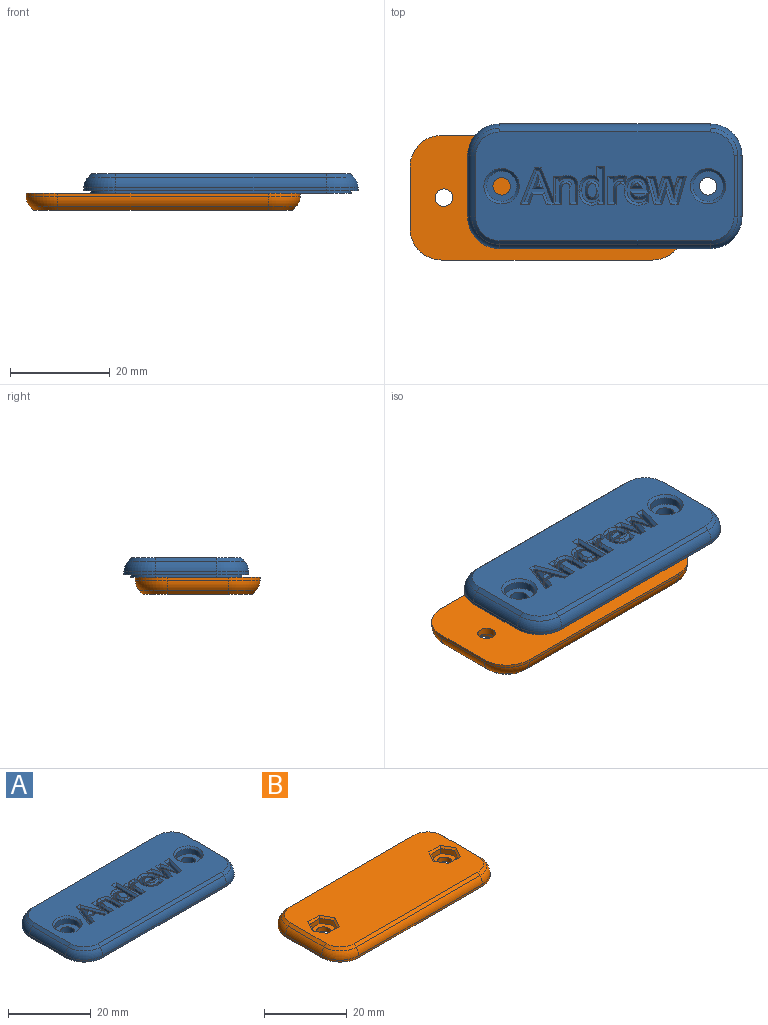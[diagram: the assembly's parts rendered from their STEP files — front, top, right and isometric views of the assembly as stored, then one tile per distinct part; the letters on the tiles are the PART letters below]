
ASSEMBLY  parts=2 mates=1
PART A: 259 faces, bbox 56.4x26.4x4.5 mm
  f0: plane 6.36x5.62mm, normal (0,0,1), area 10.3mm2, adj f87,f88,f89,f90,f91,f92,f93,f99
  f1: plane 4.93x4.02mm, normal (0,0,1), area 9mm2, adj f62,f63,f64,f65,f66,f67,f68,f69
  f2: plane 6.83x4.18mm, normal (0,0,1), area 11mm2, adj f26,f27,f28,f29,f30,f31,f32,f33
  f3: plane 12.3x0.56mm, normal (-1,0,0), area 6.9mm2, adj f4,f100,f102,f114
  f4: cylinder r=6.35mm len=6.35mm, axis (0,0,-1), area 5.6mm2, adj f3,f5,f102,f112
  f5: plane 42.3x0.56mm, normal (0,-1,0), area 23.6mm2, adj f4,f6,f102,f111
  f6: cylinder r=6.35mm len=6.35mm, axis (0,0,-1), area 5.6mm2, adj f5,f7,f102,f113
  f7: plane 12.3x0.56mm, normal (1,0,0), area 6.9mm2, adj f6,f8,f102,f115
  f8: cylinder r=6.35mm len=6.35mm, axis (0,0,-1), area 5.6mm2, adj f7,f9,f102,f117
  f9: plane 42.3x0.56mm, normal (0,1,0), area 23.6mm2, adj f8,f100,f102,f118
  f10: plane 2.9x0.72mm, normal (0,1,0), area 2.1mm2, adj f11,f94,f136,f207
  f11: plane 3.07x2.9mm, normal (1,0,0), area 8.9mm2, adj f10,f12,f136,f211
  f12: extruded ~2.9x0.87mm, area 2.7mm2, adj f11,f13,f136,f215
  f13: extruded ~2.9x0.83mm, area 2.6mm2, adj f12,f14,f136,f219
  f14: extruded ~2.9x1.09mm, area 3.5mm2, adj f13,f15,f136,f223
  f15: extruded ~2.9x1.33mm, area 4.1mm2, adj f14,f16,f136,f226
  f16: plane 2.9x2.49mm, normal (-1,0,0), area 7.2mm2, adj f15,f17,f136,f228
  f17: plane 2.9x0.72mm, normal (0,1,0), area 2.1mm2, adj f16,f18,f136,f227
  f18: plane 4.75x2.9mm, normal (1,0,0), area 13.8mm2, adj f17,f19,f136,f225
  f19: plane 2.9x0.59mm, normal (0,-1,0), area 1.7mm2, adj f18,f20,f136,f222
  f20: plane 2.9x0.65mm, normal (-0.98,-0.18,0), area 1.9mm2, adj f19,f21,f136,f218
  f21: plane 2.92x0.04mm, normal (0,-1,0), area 0mm2, adj f20,f22,f136,f218
  f22: extruded ~2.9x0.62mm, area 2.4mm2, adj f21,f23,f136,f214
  f23: extruded ~2.9x0.89mm, area 2.7mm2, adj f22,f24,f136,f210
  f24: extruded ~2.9x1.29mm, area 4mm2, adj f23,f25,f136,f206
  f25: extruded ~2.9x1.33mm, area 4.2mm2, adj f24,f94,f136,f204
  f26: plane 2.9x0.64mm, normal (0.99,0.15,0), area 1.9mm2, adj f2,f27,f95,f245
  f27: plane 2.92x0.04mm, normal (0,1,0), area 0.1mm2, adj f2,f26,f28,f245,f247
  f28: extruded ~2.9x1.49mm, area 5mm2, adj f2,f27,f29,f247
  f29: extruded ~2.9x1.45mm, area 4.8mm2, adj f2,f28,f30,f246
  f30: extruded ~2.9x1.81mm, area 5.6mm2, adj f2,f29,f31,f244
  f31: extruded ~2.9x1.83mm, area 5.6mm2, adj f2,f30,f32,f242
  f32: extruded ~2.9x1.45mm, area 4.8mm2, adj f2,f31,f33,f240
  f33: extruded ~2.9x1.48mm, area 5mm2, adj f2,f32,f34,f238
  f34: plane 2.95x0.06mm, normal (0,-1,0), area 0.2mm2, adj f2,f33,f35,f238
  f35: plane 3x0.35mm, normal (1,0.09,0), area 1mm2, adj f2,f34,f36,f238,f257
  f36: plane 3x0.33mm, normal (1,0.05,0), area 1mm2, adj f2,f35,f37,f256
  f37: plane 3x2.03mm, normal (1,0,0), area 5.8mm2, adj f2,f36,f38,f239,f255
  f38: plane 2.9x0.72mm, normal (0,-1,0), area 2.1mm2, adj f2,f37,f39,f239
  f39: plane 6.75x2.9mm, normal (-1,0,0), area 19.6mm2, adj f2,f38,f95,f241
  f40: plane 2.9x0.85mm, normal (0,1,0), area 2.5mm2, adj f41,f96,f135,f196
  f41: plane 2.9x2.79mm, normal (0.95,0.3,0), area 8.5mm2, adj f40,f42,f135,f198
  f42: extruded ~2.9x1.16mm, area 3.5mm2, adj f41,f43,f135,f198
  f43: plane 2.88x0.03mm, normal (0,1,0), area 0.1mm2, adj f42,f44,f135,f198
  f44: extruded ~2.9x1.17mm, area 3.5mm2, adj f43,f45,f135,f198,f200
  f45: plane 2.9x2.78mm, normal (-0.95,0.31,0), area 8.5mm2, adj f44,f46,f135,f199
  f46: plane 2.9x0.83mm, normal (0,1,0), area 2.4mm2, adj f45,f47,f135,f197
  f47: plane 4.75x2.9mm, normal (0.96,0.26,0), area 14.3mm2, adj f46,f48,f135,f195
  f48: plane 2.9x0.75mm, normal (0,-1,0), area 2.2mm2, adj f47,f49,f135,f193
  f49: extruded ~2.9x2.73mm, area 8.2mm2, adj f48,f50,f135,f190
  f50: extruded ~2.9x1.26mm, area 3.7mm2, adj f49,f51,f135,f185,f186
  f51: plane 2.87x0.03mm, normal (0,-1,0), area 0.1mm2, adj f50,f52,f135,f185
  f52: extruded ~2.89x0.64mm, area 1.9mm2, adj f51,f53,f135,f185
  f53: extruded ~2.9x0.62mm, area 1.9mm2, adj f52,f54,f135,f185
  f54: plane 2.9x2.73mm, normal (0.95,-0.3,0), area 8.3mm2, adj f53,f55,f135,f185
  f55: plane 2.9x0.78mm, normal (0,-1,0), area 2.3mm2, adj f54,f56,f135,f180
  f56: plane 2.9x2.73mm, normal (-0.95,-0.3,0), area 8.3mm2, adj f55,f57,f135,f182
  f57: extruded ~2.9x1.25mm, area 3.7mm2, adj f56,f58,f135,f182
  f58: plane 2.87x0.03mm, normal (0,-1,0), area 0.1mm2, adj f57,f59,f135,f182
  f59: extruded ~2.9x0.48mm, area 1.4mm2, adj f58,f60,f135,f181,f182
  f60: extruded ~3.5x2.9mm, area 10.5mm2, adj f59,f61,f135,f187
  f61: plane 2.9x0.75mm, normal (0,-1,0), area 2.2mm2, adj f60,f96,f135,f191
  f62: extruded ~2.9x0.82mm, area 2.4mm2, adj f1,f63,f97,f168
  f63: extruded ~2.9x1.66mm, area 5.3mm2, adj f1,f62,f64,f172
  f64: extruded ~2.9x1.78mm, area 5.6mm2, adj f1,f63,f65,f176
  f65: extruded ~2.9x1.83mm, area 5.7mm2, adj f1,f64,f66,f179
  f66: extruded ~2.9x1.52mm, area 5mm2, adj f1,f65,f67,f184
  f67: extruded ~2.9x1.41mm, area 4.6mm2, adj f1,f66,f68,f189
  f68: extruded ~2.9x1.55mm, area 4.9mm2, adj f1,f67,f69,f192
  f69: plane 2.9x0.46mm, normal (-1,0,0), area 1.3mm2, adj f1,f68,f70,f188
  f70: plane 3.27x2.9mm, normal (0,1,0), area 9.5mm2, adj f1,f69,f71,f183
  f71: extruded ~2.9x1.27mm, area 4mm2, adj f1,f70,f72,f178
  f72: extruded ~2.9x1.13mm, area 3.6mm2, adj f1,f71,f73,f175
  f73: extruded ~2.9x1.52mm, area 4.5mm2, adj f1,f72,f74,f171
  f74: plane 2.9x0.64mm, normal (-1,0,0), area 1.9mm2, adj f1,f73,f97,f167
  f75: extruded ~2.9x0.82mm, area 2.5mm2, adj f76,f98,f134,f170
  f76: extruded ~2.9x0.57mm, area 1.7mm2, adj f75,f77,f134,f174
  f77: plane 2.9x0.67mm, normal (-0.99,0.15,0), area 2mm2, adj f76,f78,f134,f177
  f78: extruded ~2.9x0.52mm, area 1.5mm2, adj f77,f79,f134,f173
  f79: extruded ~2.9x0.99mm, area 3.3mm2, adj f78,f80,f134,f169
  f80: extruded ~2.9x1.17mm, area 3.7mm2, adj f79,f81,f134,f165
  f81: plane 2.9x2.55mm, normal (-1,0,0), area 7.4mm2, adj f80,f82,f134,f162
  f82: plane 2.9x0.72mm, normal (0,1,0), area 2.1mm2, adj f81,f83,f134,f160
  f83: plane 4.75x2.9mm, normal (1,0,0), area 13.8mm2, adj f82,f84,f134,f159
  f84: plane 2.9x0.59mm, normal (0,-1,0), area 1.7mm2, adj f83,f85,f134,f161
  f85: plane 2.9x0.88mm, normal (-1,-0.09,0), area 2.6mm2, adj f84,f86,f134,f163
  f86: plane 2.92x0.04mm, normal (0,-1,0), area 0mm2, adj f85,f98,f134,f163
  f87: plane 2.9x0.76mm, normal (0,1,0), area 2.2mm2, adj f0,f88,f99,f220
  f88: plane 2.9x2.02mm, normal (0.93,0.36,0), area 6.3mm2, adj f0,f87,f89,f216
  f89: plane 2.9x2.54mm, normal (0,1,0), area 7.4mm2, adj f0,f88,f90,f212
  f90: plane 2.9x2.02mm, normal (-0.93,0.36,0), area 6.3mm2, adj f0,f89,f91,f208
  f91: plane 2.9x0.75mm, normal (0,1,0), area 2.2mm2, adj f0,f90,f92,f209
  f92: plane 6.36x2.9mm, normal (0.93,-0.37,0), area 19.8mm2, adj f0,f91,f93,f213
  f93: plane 2.9x0.62mm, normal (0,-1,0), area 1.8mm2, adj f0,f92,f99,f217
  f94: plane 3.1x2.9mm, normal (-1,0,0), area 9mm2, adj f10,f25,f136,f205
  f95: plane 2.9x0.59mm, normal (0,1,0), area 1.7mm2, adj f2,f26,f39,f243
  f96: plane 4.75x2.9mm, normal (-0.96,0.27,0), area 14.3mm2, adj f40,f61,f135,f194
  f97: extruded ~2.9x0.72mm, area 2.2mm2, adj f1,f62,f74,f164
  f98: extruded ~2.9x0.72mm, area 2.8mm2, adj f75,f86,f134,f166
  f99: plane 6.36x2.9mm, normal (-0.93,-0.36,0), area 19.8mm2, adj f0,f87,f93,f221
  f100: cylinder r=6.35mm len=6.35mm, axis (0,0,-1), area 5.6mm2, adj f3,f9,f102,f116
  f101: plane 52.16x22.16mm, normal (0,0,1), area 885.9mm2, adj f103,f104,f105,f106,f107,f108,f109,f110
  f102: plane 55x25mm, normal (0,0,-1), area 202.6mm2, adj f3,f4,f5,f6,f7,f8,f9,f100
  f103: plane 42.3x0.72mm, normal (0,0.71,0.71), area 43.2mm2, adj f101,f104,f105,f118
  f104: cone r=4.75mm half-angle=45deg, axis (0,0,-1), area 8.2mm2, adj f101,f103,f106,f116
  f105: cone r=4.75mm half-angle=45deg, axis (0,0,-1), area 8.2mm2, adj f101,f103,f107,f117
  f106: plane 12.3x0.72mm, normal (-0.71,0,0.71), area 12.5mm2, adj f101,f104,f108,f114
  f107: plane 12.3x0.72mm, normal (0.71,0,0.71), area 12.5mm2, adj f101,f105,f109,f115
  f108: cone r=4.75mm half-angle=45deg, axis (0,0,-1), area 8.2mm2, adj f101,f106,f110,f112
  f109: cone r=4.75mm half-angle=45deg, axis (0,0,-1), area 8.2mm2, adj f101,f107,f110,f113
  f110: plane 42.3x0.72mm, normal (0,-0.71,0.71), area 43.2mm2, adj f101,f108,f109,f111
  f111: cylinder r=3mm len=42.3mm, axis (1,0,0), area 99.7mm2, adj f5,f110,f112,f113
  f112: torus R=3.35mm, axis (0,0,1), area 22.4mm2, adj f4,f108,f111,f114
  f113: torus R=3.35mm, axis (0,0,1), area 22.4mm2, adj f6,f109,f111,f115
  f114: cylinder r=3mm len=12.3mm, axis (0,-1,0), area 29mm2, adj f3,f106,f112,f116
  f115: cylinder r=3mm len=12.3mm, axis (0,1,0), area 29mm2, adj f7,f107,f113,f117
  f116: torus R=3.35mm, axis (0,0,1), area 22.4mm2, adj f100,f104,f114,f118
  f117: torus R=3.35mm, axis (0,0,1), area 22.4mm2, adj f8,f105,f115,f118
  f118: cylinder r=3mm len=42.3mm, axis (-1,0,0), area 99.7mm2, adj f9,f103,f116,f117
  f119: cylinder r=3.05mm len=6.1mm, axis (0,0,1), area 28.7mm2, adj f120,f253
  f120: plane 6.1x6.1mm, normal (0,0,1), area 19.6mm2, adj f119,f121
  f121: cylinder r=1.75mm len=3.5mm, axis (0,0,1), area 22mm2, adj f120,f125
  f122: cylinder r=3.05mm len=6.1mm, axis (0,0,1), area 28.7mm2, adj f123,f254
  f123: plane 6.1x6.1mm, normal (0,0,1), area 19.6mm2, adj f122,f124
  f124: cylinder r=1.75mm len=3.5mm, axis (0,0,1), area 22mm2, adj f123,f125
  f125: plane 52.2x22.2mm, normal (0,0,-1), area 1118.6mm2, adj f121,f124,f126,f127,f128,f129,f130,f131
  f126: plane 12.3x0.6mm, normal (-1,0,0), area 7.4mm2, adj f102,f125,f127,f133
  f127: cylinder r=4.95mm len=4.95mm, axis (0,0,1), area 4.7mm2, adj f102,f125,f126,f128
  f128: plane 42.3x0.6mm, normal (0,-1,0), area 25.4mm2, adj f102,f125,f127,f129
  f129: cylinder r=4.95mm len=4.95mm, axis (0,0,1), area 4.7mm2, adj f102,f125,f128,f130
  f130: plane 12.3x0.6mm, normal (1,0,0), area 7.4mm2, adj f102,f125,f129,f131
  f131: cylinder r=4.95mm len=4.95mm, axis (0,0,1), area 4.7mm2, adj f102,f125,f130,f132
  f132: plane 42.3x0.6mm, normal (0,1,0), area 25.4mm2, adj f102,f125,f131,f133
  f133: cylinder r=4.95mm len=4.95mm, axis (0,0,1), area 4.7mm2, adj f102,f125,f126,f132
  f134: plane 4.84x2.74mm, normal (0,0,1), area 4.7mm2, adj f75,f76,f77,f78,f79,f80,f81,f82
  f135: plane 6.71x4.75mm, normal (0,0,1), area 12.4mm2, adj f40,f41,f42,f43,f44,f45,f46,f47
  f136: plane 4.84x3.97mm, normal (0,0,1), area 8.2mm2, adj f10,f11,f12,f13,f14,f15,f16,f17
  f137: plane 2.94x1.93mm, normal (0,0,1), area 4mm2, adj f229,f230,f231,f232,f233,f234,f235,f236
  f138: extruded ~2.9x0.98mm, area 3.3mm2, adj f2,f139,f146,f231
  f139: extruded ~2.9x1.37mm, area 4.2mm2, adj f2,f138,f140,f229
  f140: extruded ~2.9x1.39mm, area 4.2mm2, adj f2,f139,f141,f230
  f141: extruded ~2.9x0.97mm, area 3.3mm2, adj f2,f140,f142,f232
  f142: extruded ~2.9x1.07mm, area 3.5mm2, adj f2,f141,f143,f234
  f143: extruded ~2.9x1.44mm, area 4.4mm2, adj f2,f142,f144,f236
  f144: plane 2.9x0.15mm, normal (1,0,0), area 0.4mm2, adj f2,f143,f145,f237
  f145: extruded ~2.9x1.29mm, area 3.9mm2, adj f2,f144,f146,f235
  f146: extruded ~2.9x1.07mm, area 3.4mm2, adj f2,f138,f145,f233
  f147: plane 1.34x0.47mm, normal (0,0,1), area 0.4mm2, adj f248,f249,f250,f251,f252
  f148: extruded ~2.9x0.87mm, area 2.8mm2, adj f1,f149,f152,f251
  f149: extruded ~2.9x1.04mm, area 3.2mm2, adj f1,f148,f150,f252
  f150: plane 2.9x2.48mm, normal (0,-1,0), area 7.2mm2, adj f1,f149,f151,f250
  f151: extruded ~2.9x1.03mm, area 3.3mm2, adj f1,f150,f152,f248
  f152: extruded ~2.9x0.91mm, area 2.9mm2, adj f1,f148,f151,f249
  f153: plane 0.94x0.71mm, normal (0,0,1), area 0.3mm2, adj f201,f202,f258
  f154: plane 2.9x2.05mm, normal (0,-1,0), area 5.9mm2, adj f0,f155,f158,f201
  f155: plane 2.9x1.96mm, normal (-0.94,0.35,0), area 6.1mm2, adj f0,f154,f156,f202
  f156: extruded ~2.9x0.91mm, area 2.8mm2, adj f0,f155,f157,f203
  f157: extruded ~3x0.91mm, area 2.9mm2, adj f0,f156,f158,f203,f258
  f158: plane 3x1.96mm, normal (0.94,0.35,0), area 6.3mm2, adj f0,f154,f157,f201,f258
  f159: plane 5.75x0.5mm, normal (0.71,0,0.71), area 3.7mm2, adj f83,f101,f160,f161
  f160: plane 1.72x0.5mm, normal (0,0.71,0.71), area 0.9mm2, adj f82,f101,f159,f162
  f161: plane 1.55x0.5mm, normal (0,-0.71,0.71), area 0.8mm2, adj f84,f101,f159,f163
  f162: plane 3.05x0.5mm, normal (-0.71,0,0.71), area 2mm2, adj f81,f101,f160,f165
  f163: plane 1.48x0.6mm, normal (-0.7,-0.07,0.71), area 0.4mm2, adj f85,f86,f101,f161,f166
  f164: bspline ~1.22x0.85mm, area 0.7mm2, adj f97,f101,f167,f168
  f165: bspline ~1.17x0.79mm, area 0.8mm2, adj f80,f101,f162,f169
  f166: bspline ~1.14x1.07mm, area 0.4mm2, adj f98,f163,f170
  f167: plane 1.74x0.51mm, normal (-0.71,0,0.71), area 0.8mm2, adj f74,f101,f164,f171
  f168: bspline ~0.93x0.57mm, area 0.6mm2, adj f62,f101,f164,f172
  f169: bspline ~0.99x0.82mm, area 0.6mm2, adj f79,f101,f165,f173
  f170: bspline ~1.1x0.75mm, area 0.7mm2, adj f75,f101,f166,f174
  f171: bspline ~2.21x1.08mm, area 1.3mm2, adj f73,f101,f167,f175
  f172: bspline ~2.03x1.15mm, area 1.4mm2, adj f63,f101,f168,f176
  f173: bspline ~1.09x0.68mm, area 0.5mm2, adj f78,f101,f169,f177
  f174: bspline ~1.19x0.66mm, area 0.6mm2, adj f76,f101,f170,f177
  f175: bspline ~1.13x0.77mm, area 0.7mm2, adj f72,f101,f171,f178
  f176: bspline ~2.13x1.12mm, area 1.5mm2, adj f64,f101,f172,f179
  f177: plane 1.67x0.68mm, normal (-0.7,0.1,0.71), area 0.8mm2, adj f77,f101,f173,f174,f179
  f178: bspline ~1.29x0.79mm, area 0.6mm2, adj f71,f101,f175,f183
  f179: bspline ~2.15x1.07mm, area 1.5mm2, adj f65,f101,f176,f177,f184
  f180: plane 1.51x0.5mm, normal (0,-0.71,0.71), area 0.8mm2, adj f55,f101,f182,f185
  f181: bspline ~0.62x0.59mm, area 0mm2, adj f59,f182,f187
  f182: plane 4.62x1.36mm, normal (-0.68,-0.21,0.71), area 2.4mm2, adj f56,f57,f58,f59,f101,f180,f181,f187
  f183: plane 3.91x0.64mm, normal (0,0.71,0.71), area 2.3mm2, adj f70,f101,f178,f188
  f184: bspline ~1.9x1.19mm, area 1.4mm2, adj f66,f101,f179,f189
  f185: plane 4.83x1.59mm, normal (0.67,-0.22,0.71), area 2.4mm2, adj f50,f51,f52,f53,f54,f101,f180,f186
  f186: bspline ~1.45x0.78mm, area 0.3mm2, adj f50,f185,f190
  f187: bspline ~4.19x1.54mm, area 2.3mm2, adj f60,f101,f181,f182,f191
  f188: plane 0.96x0.5mm, normal (-0.71,0,0.71), area 0.5mm2, adj f69,f101,f183,f192
  f189: bspline ~1.79x1.1mm, area 1.3mm2, adj f67,f101,f184,f192
  f190: bspline ~3.23x1.28mm, area 2.1mm2, adj f49,f101,f185,f186,f193
  f191: plane 1.79x0.5mm, normal (0,-0.71,0.71), area 0.9mm2, adj f61,f101,f187,f194
  f192: bspline ~1.88x1.02mm, area 1.3mm2, adj f68,f101,f188,f189,f195
  f193: plane 1.8x0.5mm, normal (0,-0.71,0.71), area 0.9mm2, adj f48,f101,f190,f195
  f194: plane 5.75x1.97mm, normal (-0.68,0.19,0.71), area 3.9mm2, adj f96,f101,f191,f196
  f195: plane 5.78x1.98mm, normal (0.68,0.19,0.71), area 3.8mm2, adj f47,f101,f192,f193,f197
  f196: plane 1.6x0.5mm, normal (0,0.71,0.71), area 0.9mm2, adj f40,f101,f194,f198
  f197: plane 1.58x0.5mm, normal (0,0.71,0.71), area 0.9mm2, adj f46,f101,f195,f199
  f198: plane 4.78x1.56mm, normal (0.67,0.21,0.71), area 2.4mm2, adj f41,f42,f43,f44,f101,f196,f199,f200
  f199: plane 3.28x1.22mm, normal (-0.67,0.22,0.71), area 2.1mm2, adj f45,f101,f197,f198,f200
  f200: bspline ~1.38x0.81mm, area 0.3mm2, adj f44,f198,f199
  f201: plane 2.05x0.5mm, normal (0,-0.71,0.71), area 1mm2, adj f153,f154,f158,f202,f258
  f202: plane 2.08x1.19mm, normal (-0.66,0.25,0.71), area 1.2mm2, adj f153,f155,f201,f203,f258
  f203: bspline ~1.18x0.79mm, area 0.3mm2, adj f156,f157,f202,f258
  f204: bspline ~1.69x0.94mm, area 1.2mm2, adj f25,f101,f205,f206
  f205: plane 3.6x0.5mm, normal (-0.71,0,0.71), area 2.4mm2, adj f94,f101,f204,f207
  f206: bspline ~1.64x0.92mm, area 1.1mm2, adj f24,f101,f204,f210
  f207: plane 1.72x0.5mm, normal (0,0.71,0.71), area 0.9mm2, adj f10,f101,f205,f211
  f208: plane 2.52x1.12mm, normal (-0.66,0.26,0.71), area 1.5mm2, adj f90,f101,f209,f212
  f209: plane 1.82x0.5mm, normal (0,0.71,0.71), area 0.9mm2, adj f91,f101,f208,f213
  f210: bspline ~1.11x0.69mm, area 0.7mm2, adj f23,f101,f206,f214
  f211: plane 3.57x0.5mm, normal (0.71,0,0.71), area 2.4mm2, adj f11,f101,f207,f215
  f212: plane 2.54x0.5mm, normal (0,0.71,0.71), area 1.6mm2, adj f89,f101,f208,f216
  f213: plane 7.36x3.24mm, normal (0.66,-0.26,0.71), area 5.2mm2, adj f92,f101,f209,f217
  f214: bspline ~1.04x1mm, area 0.4mm2, adj f22,f101,f210,f218
  f215: bspline ~0.87x0.63mm, area 0.5mm2, adj f12,f101,f211,f219
  f216: plane 2.52x1.13mm, normal (0.66,0.26,0.71), area 1.5mm2, adj f88,f101,f212,f220
  f217: plane 1.3x0.5mm, normal (0,-0.71,0.71), area 0.7mm2, adj f93,f101,f213,f221
  f218: plane 1.25x0.6mm, normal (-0.7,-0.12,0.71), area 0.3mm2, adj f20,f21,f101,f214,f222
  f219: bspline ~0.83x0.63mm, area 0.5mm2, adj f13,f101,f215,f223
  f220: plane 1.56x0.5mm, normal (0,0.71,0.71), area 0.9mm2, adj f87,f101,f216,f221,f224
  f221: plane 7.17x2.95mm, normal (-0.66,-0.26,0.71), area 5mm2, adj f99,f101,f217,f220,f225
  f222: plane 1.5x0.5mm, normal (0,-0.71,0.71), area 0.7mm2, adj f19,f101,f218,f225
  f223: bspline ~1.09x0.73mm, area 0.7mm2, adj f14,f101,f219,f226
  f224: plane 0.47x0.19mm, normal (0,0.71,0.71), area 0.1mm2, adj f101,f220,f227
  f225: plane 5.56x0.5mm, normal (0.71,0,0.71), area 3.6mm2, adj f18,f101,f221,f222,f227
  f226: bspline ~1.33x0.73mm, area 0.9mm2, adj f15,f101,f223,f228
  f227: plane 1.53x0.5mm, normal (0,0.71,0.71), area 0.8mm2, adj f17,f101,f224,f225,f228
  f228: plane 2.99x0.5mm, normal (-0.71,0,0.71), area 1.9mm2, adj f16,f101,f226,f227
  f229: bspline ~1.37x0.74mm, area 0.9mm2, adj f137,f139,f230,f231
  f230: bspline ~1.39x0.75mm, area 0.9mm2, adj f137,f140,f229,f232
  f231: bspline ~0.98x0.76mm, area 0.6mm2, adj f137,f138,f229,f233
  f232: bspline ~0.97x0.77mm, area 0.6mm2, adj f137,f141,f230,f234
  f233: bspline ~1.07x0.72mm, area 0.7mm2, adj f137,f146,f231,f235
  f234: bspline ~1.07x0.74mm, area 0.7mm2, adj f137,f142,f232,f236
  f235: bspline ~1.29x0.72mm, area 0.8mm2, adj f137,f145,f233,f237
  f236: bspline ~1.44x0.73mm, area 0.9mm2, adj f137,f143,f234,f237
  f237: plane 0.5x0.5mm, normal (0.71,0,0.71), area 0.1mm2, adj f137,f144,f235,f236
  f238: bspline ~1.91x1.23mm, area 1mm2, adj f33,f34,f35,f101,f240,f255,f256,f257
  f239: plane 1.62x0.5mm, normal (0,-0.71,0.71), area 0.8mm2, adj f37,f38,f101,f241,f255
  f240: bspline ~1.84x1.16mm, area 1.3mm2, adj f32,f101,f238,f242
  f241: plane 7.75x0.5mm, normal (-0.71,0,0.71), area 5.1mm2, adj f39,f101,f239,f243
  f242: bspline ~2.14x1.02mm, area 1.5mm2, adj f31,f101,f240,f244
  f243: plane 1.52x0.5mm, normal (0,0.71,0.71), area 0.7mm2, adj f95,f101,f241,f245
  f244: bspline ~2.13x1.02mm, area 1.5mm2, adj f30,f101,f242,f246
  f245: plane 1.14x0.5mm, normal (0.7,0.11,0.71), area 0.3mm2, adj f26,f27,f101,f243,f247
  f246: bspline ~1.84x1.15mm, area 1.3mm2, adj f29,f101,f244,f247
  f247: bspline ~1.91x1.23mm, area 1mm2, adj f27,f28,f101,f245,f246
  f248: bspline ~1.08x0.77mm, area 0.5mm2, adj f147,f151,f249,f250
  f249: bspline ~0.91x0.72mm, area 0.6mm2, adj f147,f152,f248,f251
  f250: plane 2.67x0.68mm, normal (0,-0.71,0.71), area 1.4mm2, adj f147,f150,f248,f252
  f251: bspline ~0.87x0.68mm, area 0.5mm2, adj f147,f148,f249,f252
  f252: bspline ~1.08x0.7mm, area 0.5mm2, adj f147,f149,f250,f251
  f253: cone r=3.05mm half-angle=45deg, axis (0,0,1), area 14.7mm2, adj f101,f119
  f254: cone r=3.05mm half-angle=45deg, axis (0,0,1), area 14.7mm2, adj f101,f122
  f255: plane 2.45x0.41mm, normal (0.71,0,0.71), area 1.2mm2, adj f37,f101,f238,f239,f256
  f256: plane 0.35x0.26mm, normal (0.71,0.04,0.71), area 0.1mm2, adj f36,f238,f255,f257
  f257: plane 0.25x0.11mm, normal (0.7,0.06,0.71), area 0mm2, adj f35,f238,f256
  f258: plane 2.72x1.02mm, normal (0.66,0.25,0.71), area 1.1mm2, adj f153,f157,f158,f201,f202,f203
PART B: 54 faces, bbox 56x26x3.6 mm
  f0: plane 12.3x0.56mm, normal (-1,0,0), area 6.9mm2, adj f1,f7,f9,f21
  f1: cylinder r=6.35mm len=6.35mm, axis (0,0,-1), area 5.6mm2, adj f0,f2,f9,f19
  f2: plane 42.3x0.56mm, normal (0,-1,0), area 23.6mm2, adj f1,f3,f9,f18
  f3: cylinder r=6.35mm len=6.35mm, axis (0,0,-1), area 5.6mm2, adj f2,f4,f9,f20
  f4: plane 12.3x0.56mm, normal (1,0,0), area 6.9mm2, adj f3,f5,f9,f22
  f5: cylinder r=6.35mm len=6.35mm, axis (0,0,-1), area 5.6mm2, adj f4,f6,f9,f24
  f6: plane 42.3x0.56mm, normal (0,1,0), area 23.6mm2, adj f5,f7,f9,f25
  f7: cylinder r=6.35mm len=6.35mm, axis (0,0,-1), area 5.6mm2, adj f0,f6,f9,f23
  f8: plane 51.8x21.8mm, normal (0,0,1), area 1029.8mm2, adj f10,f11,f12,f13,f14,f15,f16,f17
  f9: plane 55x25mm, normal (0,0,-1), area 1321.1mm2, adj f0,f1,f2,f3,f4,f5,f6,f7
  f10: plane 42.3x0.72mm, normal (0,0.71,0.71), area 43.2mm2, adj f8,f11,f12,f25
  f11: cone r=4.75mm half-angle=45deg, axis (0,0,-1), area 8.2mm2, adj f8,f10,f13,f23
  f12: cone r=4.75mm half-angle=45deg, axis (0,0,-1), area 8.2mm2, adj f8,f10,f14,f24
  f13: plane 12.3x0.72mm, normal (-0.71,0,0.71), area 12.5mm2, adj f8,f11,f15,f21
  f14: plane 12.3x0.72mm, normal (0.71,0,0.71), area 12.5mm2, adj f8,f12,f16,f22
  f15: cone r=4.75mm half-angle=45deg, axis (0,0,-1), area 8.2mm2, adj f8,f13,f17,f19
  f16: cone r=4.75mm half-angle=45deg, axis (0,0,-1), area 8.2mm2, adj f8,f14,f17,f20
  f17: plane 42.3x0.72mm, normal (0,-0.71,0.71), area 43.2mm2, adj f8,f15,f16,f18
  f18: cylinder r=3mm len=42.3mm, axis (1,0,0), area 99.7mm2, adj f2,f17,f19,f20
  f19: torus R=3.35mm, axis (0,0,1), area 22.4mm2, adj f1,f15,f18,f21
  f20: torus R=3.35mm, axis (0,0,1), area 22.4mm2, adj f3,f16,f18,f22
  f21: cylinder r=3mm len=12.3mm, axis (0,-1,0), area 29mm2, adj f0,f13,f19,f23
  f22: cylinder r=3mm len=12.3mm, axis (0,1,0), area 29mm2, adj f4,f14,f20,f24
  f23: torus R=3.35mm, axis (0,0,1), area 22.4mm2, adj f7,f11,f21,f25
  f24: torus R=3.35mm, axis (0,0,1), area 22.4mm2, adj f5,f12,f22,f25
  f25: cylinder r=3mm len=42.3mm, axis (-1,0,0), area 99.7mm2, adj f6,f10,f23,f24
  f26: plane 2.9x1.67mm, normal (-0.87,0.5,0), area 5mm2, adj f27,f31,f32,f47
  f27: plane 2.9x1.67mm, normal (-0.87,-0.5,0), area 5mm2, adj f26,f28,f32,f46
  f28: plane 3.35x1.5mm, normal (0,-1,0), area 5mm2, adj f27,f29,f32,f44
  f29: plane 2.9x1.67mm, normal (0.87,-0.5,0), area 5mm2, adj f28,f30,f32,f42
  f30: plane 2.9x1.67mm, normal (0.87,0.5,0), area 5mm2, adj f29,f31,f32,f43
  f31: plane 3.35x1.5mm, normal (0,1,0), area 5mm2, adj f26,f30,f32,f45
  f32: plane 6.7x5.8mm, normal (0,0,1), area 19.5mm2, adj f26,f27,f28,f29,f30,f31,f33
  f33: cylinder r=1.75mm len=3.5mm, axis (0,0,1), area 15.4mm2, adj f9,f32
  f34: plane 2.9x1.67mm, normal (-0.87,0.5,0), area 5mm2, adj f35,f39,f40,f48
  f35: plane 2.9x1.67mm, normal (-0.87,-0.5,0), area 5mm2, adj f34,f36,f40,f49
  f36: plane 3.35x1.5mm, normal (0,-1,0), area 5mm2, adj f35,f37,f40,f51
  f37: plane 2.9x1.67mm, normal (0.87,-0.5,0), area 5mm2, adj f36,f38,f40,f53
  f38: plane 2.9x1.67mm, normal (0.87,0.5,0), area 5mm2, adj f37,f39,f40,f52
  f39: plane 3.35x1.5mm, normal (0,1,0), area 5mm2, adj f34,f38,f40,f50
  f40: plane 6.7x5.8mm, normal (0,0,1), area 19.5mm2, adj f34,f35,f36,f37,f38,f39,f41
  f41: cylinder r=1.75mm len=3.5mm, axis (0,0,1), area 15.4mm2, adj f9,f40
  f42: plane 3.4x2.25mm, normal (0.61,-0.35,0.71), area 2.6mm2, adj f8,f29,f43,f44
  f43: plane 3.4x2.25mm, normal (0.61,0.35,0.71), area 2.6mm2, adj f8,f30,f42,f45
  f44: plane 3.93x0.5mm, normal (0,-0.71,0.71), area 2.6mm2, adj f8,f28,f42,f46
  f45: plane 3.93x0.5mm, normal (0,0.71,0.71), area 2.6mm2, adj f8,f31,f43,f47
  f46: plane 3.4x2.25mm, normal (-0.61,-0.35,0.71), area 2.6mm2, adj f8,f27,f44,f47
  f47: plane 3.4x2.25mm, normal (-0.61,0.35,0.71), area 2.6mm2, adj f8,f26,f45,f46
  f48: plane 3.4x2.25mm, normal (-0.61,0.35,0.71), area 2.6mm2, adj f8,f34,f49,f50
  f49: plane 3.4x2.25mm, normal (-0.61,-0.35,0.71), area 2.6mm2, adj f8,f35,f48,f51
  f50: plane 3.93x0.5mm, normal (0,0.71,0.71), area 2.6mm2, adj f8,f39,f48,f52
  f51: plane 3.93x0.5mm, normal (0,-0.71,0.71), area 2.6mm2, adj f8,f36,f49,f53
  f52: plane 3.4x2.25mm, normal (0.61,0.35,0.71), area 2.6mm2, adj f8,f38,f50,f53
  f53: plane 3.4x2.25mm, normal (0.61,-0.35,0.71), area 2.6mm2, adj f8,f37,f51,f52
PLACE A t=(23.35,7.01,8.39)mm
PLACE B rot(axis=(1,0,0),180deg) t=(23.35,-20.05,7.79)mm
MATE planar B.f9 <-> A.f125  axis (0,0,1) through (-22.59,-6.52,7.79)mm
